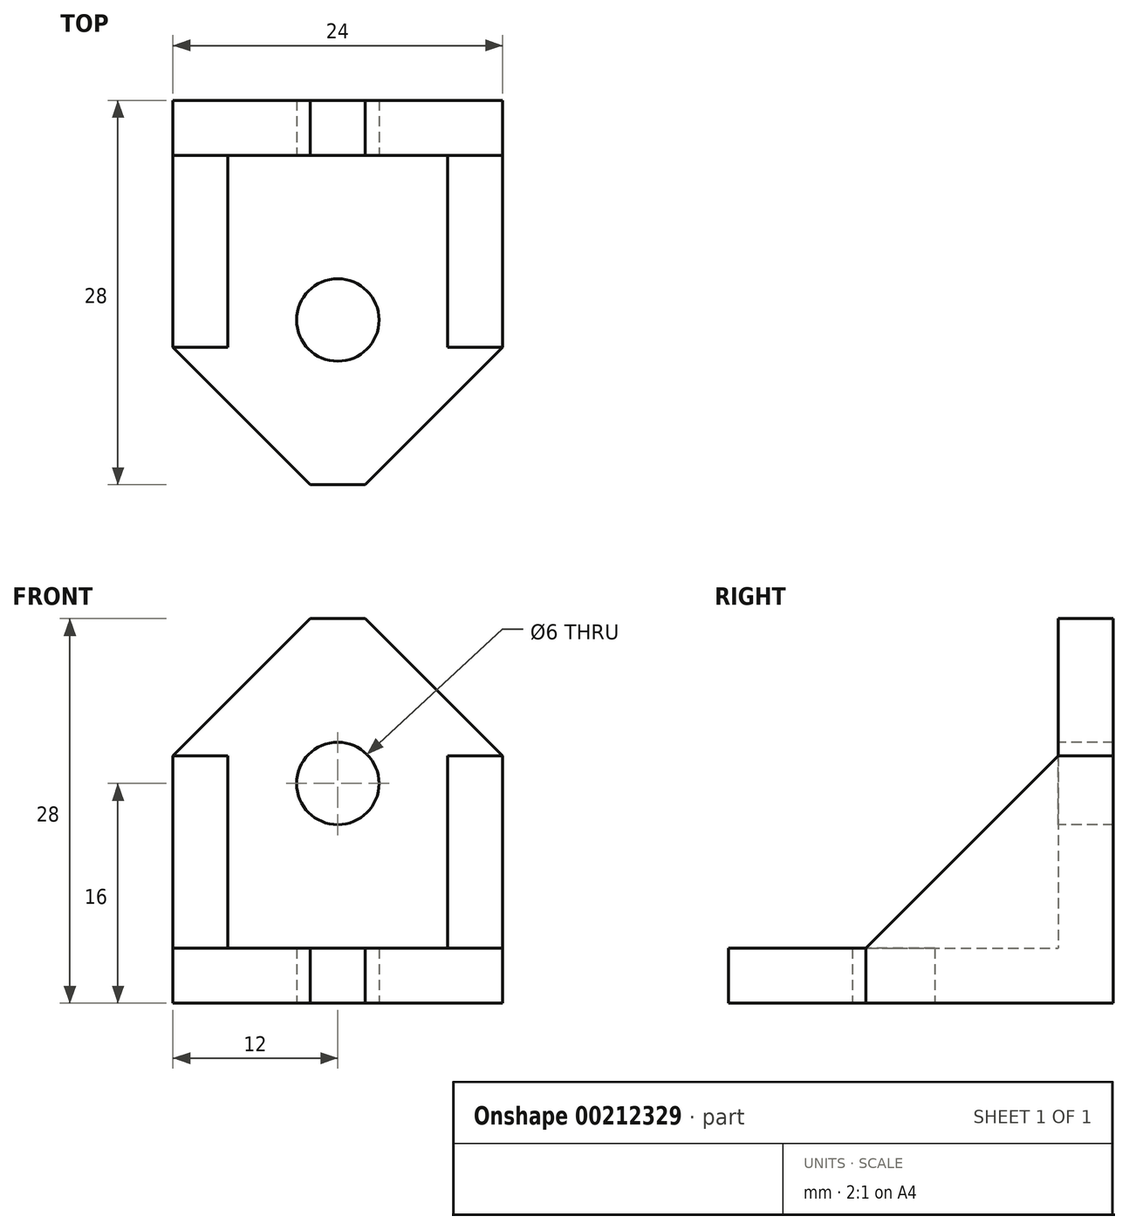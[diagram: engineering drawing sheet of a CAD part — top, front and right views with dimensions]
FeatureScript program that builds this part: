
annotation { "Feature Type Name" : "Feature", "Feature Type Description" : "" }
export const myFeature = defineFeature(function(context is Context, id is Id, definition is map)
    precondition{}
    {
        {
            var Q0;
            Q0=qCreatedBy(makeId("Top.planeOp"),FACE);
            var sketch = newSketch(context, id + "F0", { "sketchPlane" : qUnion([Q0])});
            skLineSegment(sketch, "E0.bottom", {"start": v(12, 12) * mm, "end": v(-12, 12) * mm});
            skLineSegment(sketch, "E0.top", {"start": v(12, -12) * mm, "end": v(-12, -12) * mm});
            skLineSegment(sketch, "E0.left", {"start": v(12, 12) * mm, "end": v(12, -12) * mm});
            skLineSegment(sketch, "E0.right", {"start": v(-12, 12) * mm, "end": v(-12, -12) * mm});
            skPoint(sketch, "E0.middle", {"position": v(0, 0) * mm});
            skLineSegment(sketch, "E1.bottom", {"start": v(-12, 12) * mm, "end": v(12, 12) * mm});
            skLineSegment(sketch, "E1.top", {"start": v(-12, 12) * mm, "end": v(12, 12) * mm});
            skLineSegment(sketch, "E1.left", {"start": v(-12, 12) * mm, "end": v(-12, 12) * mm});
            skLineSegment(sketch, "E1.right", {"start": v(12, 12) * mm, "end": v(12, 12) * mm});
            skCircle(sketch, "E2", {"center": v(0, 0) * mm, "radius": 3 * mm});
            skSolve(sketch);
        }
        {
            var Q0;
            Q0=makeQuery(id+"F0.imprint","IMPRINT",FACE,{"disambiguationData":[TD([[makeQuery(id+"F0.imprint","IMPRINT",EDGE,{"derivedFrom":sQuery(id+"F0.wireOp",EDGE,"E0.top")}),-1.0]])]});
            extrude(context, id + "F1", {"entities" : qUnion([Q0]), "depth" : 4 * mm});
        }
        {
            var Q0;
            Q0=qCreatedBy(makeId("Top.planeOp"),FACE);
            var sketch = newSketch(context, id + "F2", { "sketchPlane" : qUnion([Q0])});
            skLineSegment(sketch, "E3", {"start": v(0, 0) * mm, "end": v(0, 12) * mm});
            skLineSegment(sketch, "E4", {"start": v(0, 12) * mm, "end": v(-12, 12) * mm});
            skLineSegment(sketch, "E5.bottom", {"start": v(-12, 12) * mm, "end": v(12, 12) * mm});
            skLineSegment(sketch, "E5.top", {"start": v(-12, 16) * mm, "end": v(12, 16) * mm});
            skLineSegment(sketch, "E5.left", {"start": v(-12, 12) * mm, "end": v(-12, 16) * mm});
            skLineSegment(sketch, "E5.right", {"start": v(12, 12) * mm, "end": v(12, 16) * mm});
            skSolve(sketch);
        }
        {
            var Q0;
            Q0=makeQuery(id+"F2.imprint","IMPRINT",FACE,{"disambiguationData":[TD([[makeQuery(id+"F2.imprint","IMPRINT",EDGE,{"derivedFrom":sQuery(id+"F2.wireOp",EDGE,"E5.top")}),-1.0]])]});
            extrude(context, id + "F3", {"entities" : qUnion([Q0]), "operationType" : NewBodyOperationType.ADD, "depth" : 28 * mm});
        }
        {
            var Q0;
            Q0=makeQuery(id+"F3.opExtrude","SWEPT_FACE",FACE,{"disambiguationData":[OSD([sQuery(id+"F2.wireOp",EDGE,"E5.bottom")])]});
            var sketch = newSketch(context, id + "F4", { "sketchPlane" : qUnion([Q0])});
            skLineSegment(sketch, "E6", {"start": v(0, 4) * mm, "end": v(0, 16) * mm});
            skPoint(sketch, "E6.endSnap0", {"position": v(0, 4) * mm});
            skCircle(sketch, "E7", {"center": v(0, 16) * mm, "radius": 3 * mm});
            skSolve(sketch);
        }
        {
            var Q0;
            Q0 = qSketchRegion(id + "F4", true);
            extrude(context, id + "F5", {"entities" : qUnion([Q0]), "operationType" : NewBodyOperationType.REMOVE, "oppositeDirection" : true, "depth" : 25 * mm});
        }
        {
            var Q0;
            Q0=makeQuery(id+"F1.opExtrude","SWEPT_EDGE",EDGE,{"disambiguationData":[OSD([sQuery(id+"F0.wireOp",EDGE,"E0.top"),sQuery(id+"F0.wireOp",EDGE,"E0.right")])]});
            var Q1;
            Q1=makeQuery(id+"F1.opExtrude","SWEPT_EDGE",EDGE,{"disambiguationData":[OSD([sQuery(id+"F0.wireOp",EDGE,"E0.top"),sQuery(id+"F0.wireOp",EDGE,"E0.left")])]});
            var Q2;
            Q2=makeQuery(id+"F3.opExtrude","CAP_EDGE",EDGE,{"disambiguationData":[OSD([sQuery(id+"F2.wireOp",EDGE,"E5.left")])],"isStart":false});
            var Q3;
            Q3=makeQuery(id+"F3.opExtrude","CAP_EDGE",EDGE,{"disambiguationData":[OSD([sQuery(id+"F2.wireOp",EDGE,"E5.right")])],"isStart":false});
            chamfer(context, id + "F6", {"entities" : qUnion([Q0, Q1, Q2, Q3]), "width" : 10 * mm, "tangentPropagation" : true});
        }
        {
            var Q0;
            Q0=makeQuery(id+"F1.opExtrude","CAP_FACE",FACE,{"disambiguationData":[OSD([sQuery(id+"F0.wireOp",EDGE,"E0.top"),sQuery(id+"F0.wireOp",EDGE,"E0.left"),sQuery(id+"F0.wireOp",EDGE,"E0.right"),sQuery(id+"F0.wireOp",EDGE,"E1.top"),sQuery(id+"F0.wireOp",EDGE,"E2")])],"isStart":false});
            var sketch = newSketch(context, id + "F7", { "sketchPlane" : qUnion([Q0])});
            skLineSegment(sketch, "E8.bottom", {"start": v(-12, -2) * mm, "end": v(-8, -2) * mm});
            skLineSegment(sketch, "E8.top", {"start": v(-12, 12) * mm, "end": v(-8, 12) * mm});
            skLineSegment(sketch, "E8.left", {"start": v(-12, -2) * mm, "end": v(-12, 12) * mm});
            skLineSegment(sketch, "E8.right", {"start": v(-8, -2) * mm, "end": v(-8, 12) * mm});
            skLineSegment(sketch, "E9.bottom", {"start": v(12, -2) * mm, "end": v(8, -2) * mm});
            skLineSegment(sketch, "E9.top", {"start": v(12, 12) * mm, "end": v(8, 12) * mm});
            skLineSegment(sketch, "E9.left", {"start": v(12, -2) * mm, "end": v(12, 12) * mm});
            skLineSegment(sketch, "E9.right", {"start": v(8, -2) * mm, "end": v(8, 12) * mm});
            skSolve(sketch);
        }
        {
            var Q0;
            Q0=makeQuery(id+"F7.imprint","IMPRINT",FACE,{"disambiguationData":[TD([[makeQuery(id+"F7.imprint","IMPRINT",EDGE,{"derivedFrom":sQuery(id+"F7.wireOp",EDGE,"E8.bottom")}),1.0]])]});
            var Q1;
            Q1=makeQuery(id+"F7.imprint","IMPRINT",FACE,{"disambiguationData":[TD([[makeQuery(id+"F7.imprint","IMPRINT",EDGE,{"derivedFrom":sQuery(id+"F7.wireOp",EDGE,"E9.bottom")}),-1.0]])]});
            extrude(context, id + "F8", {"entities" : qUnion([Q0, Q1]), "operationType" : NewBodyOperationType.ADD, "depth" : 14 * mm});
        }
        {
            var Q0;
            Q0=makeQuery(id+"F8.opExtrude","CAP_EDGE",EDGE,{"disambiguationData":[OSD([sQuery(id+"F7.wireOp",EDGE,"E8.bottom")])],"isStart":false});
            var Q1;
            Q1=makeQuery(id+"F8.opExtrude","CAP_EDGE",EDGE,{"disambiguationData":[OSD([sQuery(id+"F7.wireOp",EDGE,"E9.bottom")])],"isStart":false});
            chamfer(context, id + "F9", {"entities" : qUnion([Q0, Q1]), "width" : 14 * mm, "tangentPropagation" : true});
        }
    });
